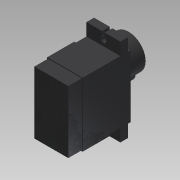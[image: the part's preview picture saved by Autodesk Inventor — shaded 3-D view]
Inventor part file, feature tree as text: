
AUTODESK INVENTOR PART (.ipt)
format: ipt  version: 2015 (Build 190159000, 159)  size: 254,464 bytes
history: native  units: mm
features: extrude x13, sketch x13, projected_geometry x5
ambient origin geometry x8: Origin, YZ Plane, XZ Plane, XY Plane, X Axis, Y Axis, Z Axis, Center Point
bodies: Solid1 (feature_tree)
feature tree (31):
  extrude  "Extrusion1"  Depth=23.0mm
  extrude  "Extrusion2"  Depth=32.2mm
  extrude  "Extrusion3"  Depth=1.0mm TaperAngle=0.0deg
  extrude  "Extrusion4"  Depth=5.5mm TaperAngle=0.0deg
  extrude  "Extrusion5"  Depth=2.8mm TaperAngle=0.0deg
  extrude  "Extrusion6"  Depth=2.0mm TaperAngle=0.0deg
  extrude  "Extrusion7"  Depth=2.0mm TaperAngle=0.0deg
  extrude  "Extrusion8"  Depth=5.0mm
  extrude  "Extrusion9"  Depth=5.0mm
  extrude  "Extrusion11"  Depth=0.3mm TaperAngle=0.0deg
  extrude  "Extrusion12"  Depth=0.3mm TaperAngle=0.0deg
  extrude  "Extrusion13"  Depth=0.3mm TaperAngle=0.0deg
  extrude  "Extrusion14"  [1 undecoded]
  sketch  "Sketch1"  dims[d0=12.5mm d1=23.0mm]
  sketch  "Sketch2"  dims[d2=23.0mm d3=0.0mm d4=32.2mm]
  sketch  "Sketch3"  dims[d5=3.8mm d6=0.0mm d7=1.0mm d8=0.0mm]
  sketch  "Sketch4"  dims[d9=6.25mm d10=5.5mm d11=0.0mm]
  sketch  "Sketch5"  dims[d14=2.8mm d15=7.5mm d16=0.0mm]
  sketch  "Sketch6"  dims[d17=6.95mm d18=2.0mm d19=0.0mm]
  sketch  "Sketch7"  dims[d20=7.0mm d21=2.0mm d22=0.0mm]
  sketch  "Sketch8"  dims[d27=10.0mm d28=0.0mm d29=5.0mm]
  projected_geometry  "Projected Loop1"
  projected_geometry  "Projected Loop2"
  sketch  "Sketch9"  dims[d30=10.0mm d31=0.0mm d32=5.0mm]
  projected_geometry  "Projected Loop3"
  sketch  "Sketch10"  dims[d33=10.0mm d36=0.3mm d37=0.0mm]
  projected_geometry  "Projected Loop4"
  sketch  "Sketch11"  dims[d38=0.3mm d39=0.3mm d40=0.0mm]
  sketch  "Sketch12"  dims[d41=0.3mm d42=0.3mm d43=0.0mm]
  projected_geometry  "Projected Loop5"
  sketch  "Sketch13"  dims[d44=0.3mm d45=0.0mm]
note: 1 required parameter value undecoded (feature->parameter linkage not recoverable at this tier; creation-order binding heuristic only, values carry confidence <= 0.55)
